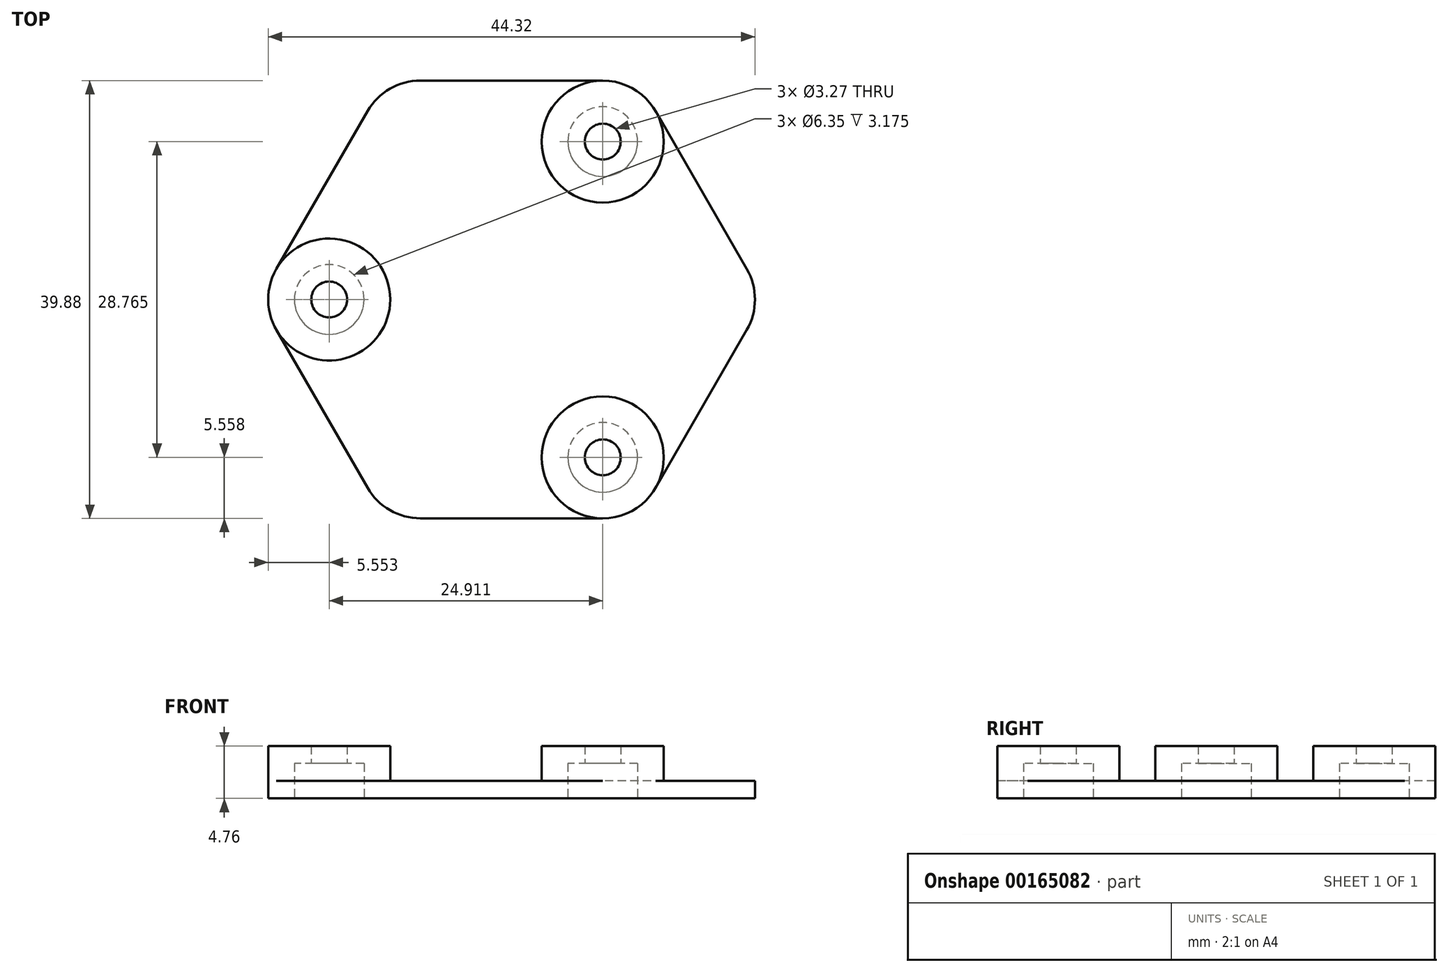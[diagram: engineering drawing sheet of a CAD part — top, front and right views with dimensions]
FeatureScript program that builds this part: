
annotation { "Feature Type Name" : "Feature", "Feature Type Description" : "" }
export const myFeature = defineFeature(function(context is Context, id is Id, definition is map)
    precondition{}
    {
        {
            var Q0;
            Q0=qCreatedBy(makeId("Top.planeOp"),FACE);
            var sketch = newSketch(context, id + "F0", { "sketchPlane" : qUnion([Q0])});
            skCircle(sketch, "E0.cCircle", {"center": v(0, 0) * mm, "radius": 14.38 * mm, "construction": true});
            skLineSegment(sketch, "E0.0", {"start": v(-8.3, 14.38) * mm, "end": v(8.3, 14.38) * mm, "construction": true});
            skLineSegment(sketch, "E0.1", {"start": v(8.3, 14.38) * mm, "end": v(16.6, 0) * mm, "construction": true});
            skLineSegment(sketch, "E0.2", {"start": v(16.6, 0) * mm, "end": v(8.3, -14.38) * mm, "construction": true});
            skLineSegment(sketch, "E0.3", {"start": v(8.3, -14.38) * mm, "end": v(-8.3, -14.38) * mm, "construction": true});
            skLineSegment(sketch, "E0.4", {"start": v(-8.3, -14.38) * mm, "end": v(-16.6, 0) * mm, "construction": true});
            skLineSegment(sketch, "E0.5", {"start": v(-16.6, 0) * mm, "end": v(-8.3, 14.38) * mm, "construction": true});
            skPoint(sketch, "E0.0.midPoint", {"position": v(0, 14.38) * mm});
            skCircle(sketch, "E1.cCircle", {"center": v(0, 0) * mm, "radius": 19.94 * mm, "construction": true});
            skLineSegment(sketch, "E1.0", {"start": v(-11.51, 19.94) * mm, "end": v(11.51, 19.94) * mm});
            skLineSegment(sketch, "E1.1", {"start": v(11.51, 19.94) * mm, "end": v(23.02, 0) * mm});
            skLineSegment(sketch, "E1.2", {"start": v(23.02, 0) * mm, "end": v(11.51, -19.94) * mm});
            skLineSegment(sketch, "E1.3", {"start": v(11.51, -19.94) * mm, "end": v(-11.51, -19.94) * mm});
            skLineSegment(sketch, "E1.4", {"start": v(-11.51, -19.94) * mm, "end": v(-23.02, 0) * mm});
            skLineSegment(sketch, "E1.5", {"start": v(-23.02, 0) * mm, "end": v(-11.51, 19.94) * mm});
            skPoint(sketch, "E1.0.midPoint", {"position": v(0, 19.94) * mm});
            skCircle(sketch, "E2", {"center": v(-8.3, 14.38) * mm, "radius": 5.56 * mm, "construction": true});
            skLineSegment(sketch, "E3", {"start": v(-8.3, 14.38) * mm, "end": v(0, 0) * mm, "construction": true});
            skCircle(sketch, "E4", {"center": v(8.3, 14.38) * mm, "radius": 1.63 * mm});
            skCircle(sketch, "E5", {"center": v(-16.6, 0) * mm, "radius": 1.63 * mm});
            skCircle(sketch, "E6", {"center": v(8.3, -14.38) * mm, "radius": 1.63 * mm});
            skSolve(sketch);
        }
        {
            var Q0;
            Q0 = qSketchRegion(id + "F0", true);
            extrude(context, id + "F1", {"entities" : qUnion([Q0]), "depth" : 1.59 * mm});
        }
        {
            var Q0;
            Q0=makeQuery(id+"F1.opExtrude","SWEPT_EDGE",EDGE,{"disambiguationData":[OSD([sQuery(id+"F0.wireOp",EDGE,"E1.4"),sQuery(id+"F0.wireOp",EDGE,"E1.5")])]});
            var Q1;
            Q1=makeQuery(id+"F1.opExtrude","SWEPT_EDGE",EDGE,{"disambiguationData":[OSD([sQuery(id+"F0.wireOp",EDGE,"E1.3"),sQuery(id+"F0.wireOp",EDGE,"E1.4")])]});
            var Q2;
            Q2=makeQuery(id+"F1.opExtrude","SWEPT_EDGE",EDGE,{"disambiguationData":[OSD([sQuery(id+"F0.wireOp",EDGE,"E1.2"),sQuery(id+"F0.wireOp",EDGE,"E1.3")])]});
            var Q3;
            Q3=makeQuery(id+"F1.opExtrude","SWEPT_EDGE",EDGE,{"disambiguationData":[OSD([sQuery(id+"F0.wireOp",EDGE,"E1.1"),sQuery(id+"F0.wireOp",EDGE,"E1.2")])]});
            var Q4;
            Q4=makeQuery(id+"F1.opExtrude","SWEPT_EDGE",EDGE,{"disambiguationData":[OSD([sQuery(id+"F0.wireOp",EDGE,"E1.0"),sQuery(id+"F0.wireOp",EDGE,"E1.1")])]});
            var Q5;
            Q5=makeQuery(id+"F1.opExtrude","SWEPT_EDGE",EDGE,{"disambiguationData":[OSD([sQuery(id+"F0.wireOp",EDGE,"E1.0"),sQuery(id+"F0.wireOp",EDGE,"E1.5")])]});
            fillet(context, id + "F2", {"entities" : qUnion([Q0, Q1, Q2, Q3, Q4, Q5]), "radius" : 5.56 * mm, "tangentPropagation" : true, "allowEdgeOverflow" : false});
        }
        {
            var Q0;
            Q0=makeQuery(id+"F1.opExtrude","CAP_FACE",FACE,{"disambiguationData":[OSD([sQuery(id+"F0.wireOp",EDGE,"E1.0"),sQuery(id+"F0.wireOp",EDGE,"E1.1"),sQuery(id+"F0.wireOp",EDGE,"E1.2"),sQuery(id+"F0.wireOp",EDGE,"E1.3"),sQuery(id+"F0.wireOp",EDGE,"E1.4"),sQuery(id+"F0.wireOp",EDGE,"E1.5"),sQuery(id+"F0.wireOp",EDGE,"E4"),sQuery(id+"F0.wireOp",EDGE,"E5"),sQuery(id+"F0.wireOp",EDGE,"E6")])],"isStart":false});
            var sketch = newSketch(context, id + "F3", { "sketchPlane" : qUnion([Q0])});
            skCircle(sketch, "E7", {"center": v(8.3, -14.38) * mm, "radius": 5.56 * mm});
            skCircle(sketch, "E8", {"center": v(8.3, -14.38) * mm, "radius": 1.63 * mm});
            skCircle(sketch, "E9", {"center": v(8.3, 14.38) * mm, "radius": 5.56 * mm});
            skCircle(sketch, "E10", {"center": v(8.3, 14.38) * mm, "radius": 1.63 * mm});
            skCircle(sketch, "E11", {"center": v(-16.6, 0) * mm, "radius": 1.63 * mm});
            skCircle(sketch, "E12", {"center": v(-16.6, 0) * mm, "radius": 5.56 * mm});
            skSolve(sketch);
        }
        {
            var Q0;
            Q0 = qSketchRegion(id + "F3", true);
            extrude(context, id + "F4", {"entities" : qUnion([Q0]), "operationType" : NewBodyOperationType.ADD, "depth" : 3.17 * mm});
        }
        {
            var Q0;
            Q0=makeQuery(id+"F4.opExtrude","CAP_FACE",FACE,{"disambiguationData":[OSD([sQuery(id+"F3.wireOp",EDGE,"E7"),sQuery(id+"F3.wireOp",EDGE,"E8")])],"isStart":false});
            cPlane(context, id + "F5", {"entities" : qUnion([Q0]), "cplaneType" : CPlaneType.OFFSET, "offset" : 1.59 * mm, "oppositeDirection" : true, "width" : 152.4 * mm, "height" : 152.4 * mm});
        }
        {
            var Q0;
            Q0=makeQuery(id+"F1.opExtrude","CAP_FACE",FACE,{"disambiguationData":[OSD([sQuery(id+"F0.wireOp",EDGE,"E1.0"),sQuery(id+"F0.wireOp",EDGE,"E1.1"),sQuery(id+"F0.wireOp",EDGE,"E1.2"),sQuery(id+"F0.wireOp",EDGE,"E1.3"),sQuery(id+"F0.wireOp",EDGE,"E1.4"),sQuery(id+"F0.wireOp",EDGE,"E1.5"),sQuery(id+"F0.wireOp",EDGE,"E4"),sQuery(id+"F0.wireOp",EDGE,"E5"),sQuery(id+"F0.wireOp",EDGE,"E6")])],"isStart":true});
            var sketch = newSketch(context, id + "F6", { "sketchPlane" : qUnion([Q0])});
            skCircle(sketch, "E13", {"center": v(8.3, 14.38) * mm, "radius": 3.18 * mm});
            skCircle(sketch, "E14", {"center": v(8.3, -14.38) * mm, "radius": 3.18 * mm});
            skCircle(sketch, "E15", {"center": v(-16.6, 0) * mm, "radius": 3.18 * mm});
            skSolve(sketch);
        }
        {
            var Q0;
            Q0 = qSketchRegion(id + "F6", true);
            var Q1;
            Q1=qCreatedBy(id+"F5.planeOp",FACE);
            extrude(context, id + "F7", {"entities" : qUnion([Q0]), "operationType" : NewBodyOperationType.REMOVE, "endBound" : BoundingType.UP_TO_SURFACE, "oppositeDirection" : true, "endBoundEntityFace" : qUnion([Q1]), "depth" : 25.4 * mm});
        }
    });
